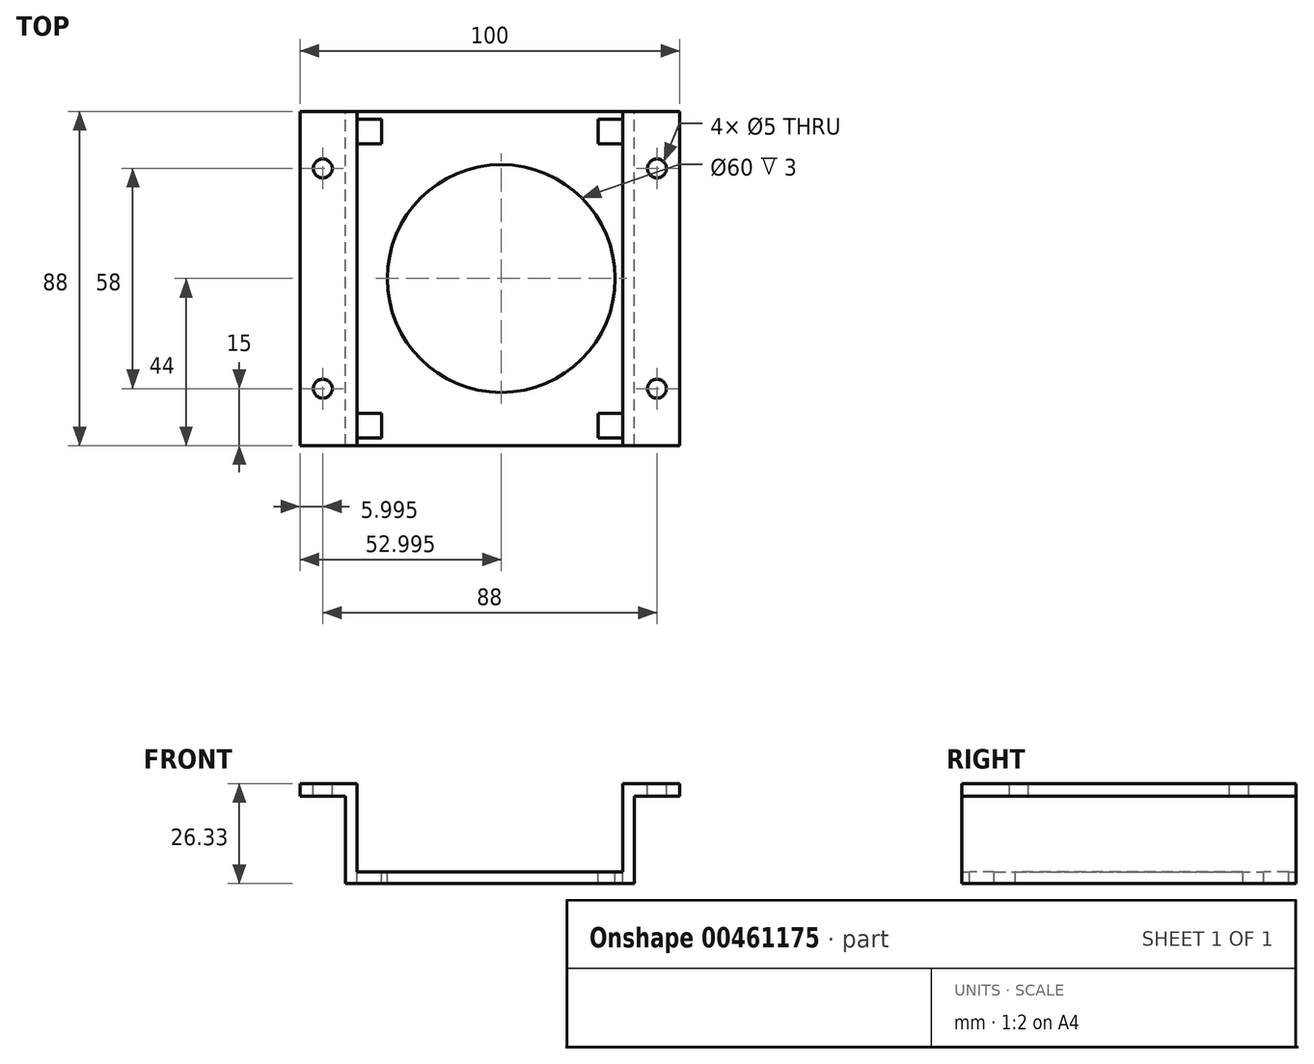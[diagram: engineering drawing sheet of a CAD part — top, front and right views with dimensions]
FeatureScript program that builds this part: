
annotation { "Feature Type Name" : "Feature", "Feature Type Description" : "" }
export const myFeature = defineFeature(function(context is Context, id is Id, definition is map)
    precondition{}
    {
        {
            var Q0;
            Q0=qCreatedBy(makeId("Front.planeOp"),FACE);
            var sketch = newSketch(context, id + "F0", { "sketchPlane" : qUnion([Q0])});
            skLineSegment(sketch, "E0", {"start": v(-1.97, -2.2) * mm, "end": v(-1.97, -5.2) * mm});
            skLineSegment(sketch, "E1", {"start": v(-1.97, -5.2) * mm, "end": v(36.03, -5.2) * mm});
            skLineSegment(sketch, "E2", {"start": v(36.03, -5.2) * mm, "end": v(36.03, 17.8) * mm});
            skLineSegment(sketch, "E3", {"start": v(36.03, 17.8) * mm, "end": v(48.03, 17.8) * mm});
            skLineSegment(sketch, "E4", {"start": v(48.03, 17.8) * mm, "end": v(48.03, 21.12) * mm});
            skLineSegment(sketch, "E5", {"start": v(48.03, 21.12) * mm, "end": v(33.03, 21.12) * mm});
            skLineSegment(sketch, "E6", {"start": v(33.03, 21.12) * mm, "end": v(33.03, -2.2) * mm});
            skLineSegment(sketch, "E7", {"start": v(33.03, -2.2) * mm, "end": v(-1.97, -2.2) * mm});
            skLineSegment(sketch, "E8.MirrorCS", {"start": v(-51.97, 17.8) * mm, "end": v(-51.97, 21.12) * mm});
            skLineSegment(sketch, "E9.MirrorCS", {"start": v(-39.97, -5.2) * mm, "end": v(-39.97, 17.8) * mm});
            skLineSegment(sketch, "E10.MirrorCS", {"start": v(-39.97, 17.8) * mm, "end": v(-51.97, 17.8) * mm});
            skLineSegment(sketch, "E11.MirrorCS", {"start": v(-51.97, 21.12) * mm, "end": v(-36.97, 21.12) * mm});
            skLineSegment(sketch, "E12.MirrorCS", {"start": v(-36.97, 21.12) * mm, "end": v(-36.97, -2.2) * mm});
            skLineSegment(sketch, "E13.MirrorCS", {"start": v(-1.97, -5.2) * mm, "end": v(-39.97, -5.2) * mm});
            skLineSegment(sketch, "E14.MirrorCS", {"start": v(-36.97, -2.2) * mm, "end": v(-1.97, -2.2) * mm});
            skPoint(sketch, "E15.MirrorCS.start.orphan", {"position": v(36.03, 17.8) * mm});
            skSolve(sketch);
        }
        {
            var Q0;
            Q0=qSketchRegion(id+"F0",true);
            extrude(context, id + "F1", {"entities" : qUnion([Q0]), "endBound" : BoundingType.SYMMETRIC, "depth" : 88 * mm});
        }
        {
            var Q0;
            Q0=makeQuery(id+"F1.opExtrude","SWEPT_FACE",FACE,{"disambiguationData":[OSD([sQuery(id+"F0.wireOp",EDGE,"E5")])]});
            var sketch = newSketch(context, id + "F2", { "sketchPlane" : qUnion([Q0])});
            skLineSegment(sketch, "E16", {"start": v(42.03, -44) * mm, "end": v(42.03, 34) * mm, "construction": true});
            skLineSegment(sketch, "E17.0.0", {"start": v(-36.97, 44) * mm, "end": v(-51.97, 44) * mm, "construction": true});
            skLineSegment(sketch, "E17.0.1", {"start": v(-51.97, 44) * mm, "end": v(-51.97, -44) * mm, "construction": true});
            skLineSegment(sketch, "E17.0.2", {"start": v(-51.97, -44) * mm, "end": v(-36.97, -44) * mm, "construction": true});
            skLineSegment(sketch, "E17.0.3", {"start": v(-36.97, -44) * mm, "end": v(-36.97, 44) * mm, "construction": true});
            skLineSegment(sketch, "E18", {"start": v(-45.97, 34) * mm, "end": v(-45.97, -44) * mm, "construction": true});
            skLineSegment(sketch, "E19", {"start": v(-51.97, -29) * mm, "end": v(48.03, -29) * mm, "construction": true});
            skLineSegment(sketch, "E20", {"start": v(48.03, 29) * mm, "end": v(-51.97, 29) * mm, "construction": true});
            skLineSegment(sketch, "E21", {"start": v(48.03, -29) * mm, "end": v(48.03, -44) * mm, "construction": true});
            skLineSegment(sketch, "E22", {"start": v(48.03, 44) * mm, "end": v(48.03, 29) * mm, "construction": true});
            skCircle(sketch, "E23", {"center": v(42.03, -29) * mm, "radius": 2.5 * mm});
            skCircle(sketch, "E24", {"center": v(42.03, 29) * mm, "radius": 2.5 * mm});
            skCircle(sketch, "E25", {"center": v(-45.97, 29) * mm, "radius": 2.5 * mm});
            skCircle(sketch, "E26", {"center": v(-45.97, -29) * mm, "radius": 2.5 * mm});
            skSolve(sketch);
        }
        {
            var Q0;
            Q0=qSketchRegion(id+"F2",true);
            extrude(context, id + "F3", {"entities" : qUnion([Q0]), "operationType" : NewBodyOperationType.REMOVE, "endBound" : BoundingType.UP_TO_NEXT, "oppositeDirection" : true, "depth" : 25 * mm});
        }
        {
            var Q0;
            Q0=makeQuery(id+"F1.opExtrude","SWEPT_FACE",FACE,{"disambiguationData":[OSD([sQuery(id+"F0.wireOp",EDGE,"E7"),sQuery(id+"F0.wireOp",EDGE,"E14.MirrorCS")])]});
            var sketch = newSketch(context, id + "F4", { "sketchPlane" : qUnion([Q0])});
            skPoint(sketch, "E27", {"position": v(1.03, 0) * mm});
            skCircle(sketch, "E28", {"center": v(1.03, 0) * mm, "radius": 30 * mm});
            skSolve(sketch);
        }
        {
            var Q0;
            Q0 = qSketchRegion(id + "F4", true);
            extrude(context, id + "F5", {"entities" : qUnion([Q0]), "operationType" : NewBodyOperationType.REMOVE, "endBound" : BoundingType.UP_TO_NEXT, "oppositeDirection" : true, "depth" : 25 * mm});
        }
        {
            var Q0;
            Q0=makeQuery(id+"F1.opExtrude","SWEPT_FACE",FACE,{"disambiguationData":[OSD([sQuery(id+"F0.wireOp",EDGE,"E7"),sQuery(id+"F0.wireOp",EDGE,"E14.MirrorCS")])]});
            var sketch = newSketch(context, id + "F6", { "sketchPlane" : qUnion([Q0])});
            skLineSegment(sketch, "E29.bottom", {"start": v(-36.97, 42) * mm, "end": v(-30.47, 42) * mm});
            skLineSegment(sketch, "E29.top", {"start": v(-36.97, 35.5) * mm, "end": v(-30.47, 35.5) * mm});
            skLineSegment(sketch, "E29.left", {"start": v(-36.97, 42) * mm, "end": v(-36.97, 35.5) * mm});
            skLineSegment(sketch, "E29.right", {"start": v(-30.47, 42) * mm, "end": v(-30.47, 35.5) * mm});
            skLineSegment(sketch, "E30", {"start": v(-36.97, 42) * mm, "end": v(33.03, 42) * mm, "construction": true});
            skLineSegment(sketch, "E31", {"start": v(-36.97, -42) * mm, "end": v(33.03, -42) * mm, "construction": true});
            skLineSegment(sketch, "E32.bottom", {"start": v(26.53, 42) * mm, "end": v(33.03, 42) * mm});
            skLineSegment(sketch, "E32.top", {"start": v(26.53, 35.5) * mm, "end": v(33.03, 35.5) * mm});
            skLineSegment(sketch, "E32.left", {"start": v(26.53, 42) * mm, "end": v(26.53, 35.5) * mm});
            skLineSegment(sketch, "E32.right", {"start": v(33.03, 42) * mm, "end": v(33.03, 35.5) * mm});
            skLineSegment(sketch, "E33.bottom", {"start": v(33.03, -35.5) * mm, "end": v(26.53, -35.5) * mm});
            skLineSegment(sketch, "E33.top", {"start": v(33.03, -42) * mm, "end": v(26.53, -42) * mm});
            skLineSegment(sketch, "E33.left", {"start": v(33.03, -35.5) * mm, "end": v(33.03, -42) * mm});
            skLineSegment(sketch, "E33.right", {"start": v(26.53, -35.5) * mm, "end": v(26.53, -42) * mm});
            skLineSegment(sketch, "E34.bottom", {"start": v(-36.97, -35.5) * mm, "end": v(-30.47, -35.5) * mm});
            skLineSegment(sketch, "E34.top", {"start": v(-36.97, -42) * mm, "end": v(-30.47, -42) * mm});
            skLineSegment(sketch, "E34.left", {"start": v(-36.97, -35.5) * mm, "end": v(-36.97, -42) * mm});
            skLineSegment(sketch, "E34.right", {"start": v(-30.47, -35.5) * mm, "end": v(-30.47, -42) * mm});
            skSolve(sketch);
        }
        {
            var Q0;
            Q0 = qSketchRegion(id + "F6", true);
            extrude(context, id + "F7", {"entities" : qUnion([Q0]), "operationType" : NewBodyOperationType.REMOVE, "endBound" : BoundingType.UP_TO_NEXT, "oppositeDirection" : true, "depth" : 25 * mm});
        }
    });
